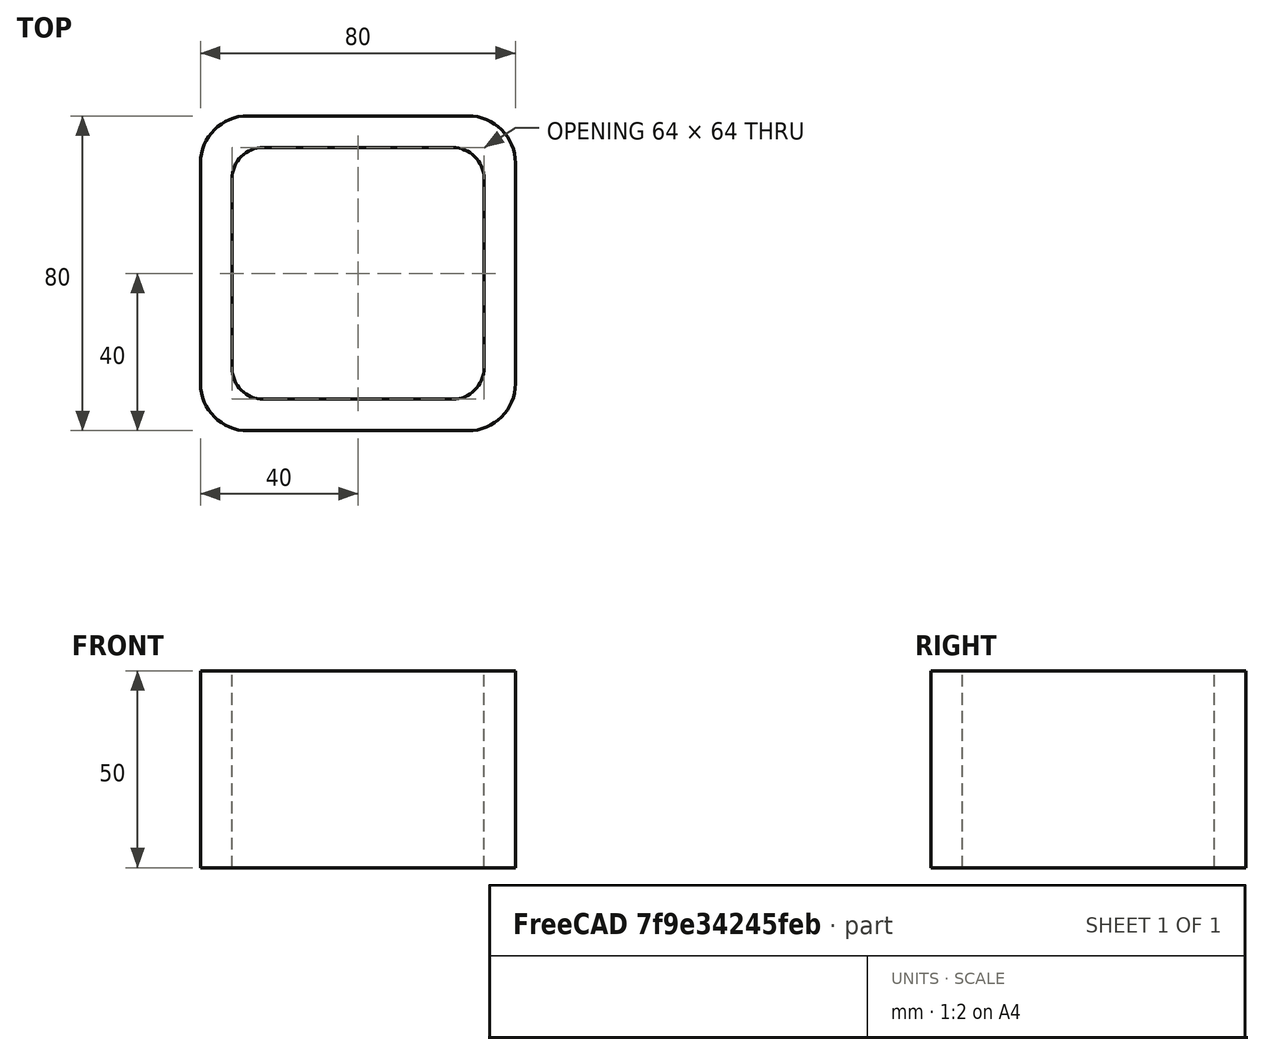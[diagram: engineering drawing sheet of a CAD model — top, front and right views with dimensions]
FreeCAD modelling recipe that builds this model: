
FCSTD DOCUMENT  (FreeCAD 0.15R4671 (Git))
Label: Square hollow section 80x80x8 EN10219 S235JRH
License: All rights reserved
LicenseURL: http://en.wikipedia.org/wiki/All_rights_reserved
objects: Sketcher::SketchObject×1, Part::Extrusion×1
note: 2 computed .brp shape members not serialized (recipe doc carries the construction recipe); baked Part::Feature solids carry a one-line shape summary decoded from their .brp

FEATURE [Sketcher::SketchObject] Sketch
  sketch-geometry (16):
    g0: LineSegment StartX=-24 StartY=32 StartZ=0 EndX=24 EndY=32 EndZ=0
    g1: LineSegment StartX=32 StartY=24 StartZ=0 EndX=32 EndY=-24 EndZ=0
    g2: LineSegment StartX=24 StartY=-32 StartZ=0 EndX=-24 EndY=-32 EndZ=0
    g3: LineSegment StartX=-32 StartY=-24 StartZ=0 EndX=-32 EndY=24 EndZ=0
    g4: LineSegment StartX=-28 StartY=40 StartZ=0 EndX=28 EndY=40 EndZ=0
    g5: LineSegment StartX=40 StartY=28 StartZ=0 EndX=40 EndY=-28 EndZ=0
    g6: LineSegment StartX=28 StartY=-40 StartZ=0 EndX=-28 EndY=-40 EndZ=0
    g7: LineSegment StartX=-40 StartY=-28 StartZ=0 EndX=-40 EndY=28 EndZ=0
    g8: ArcOfCircle CenterX=-24 CenterY=24 CenterZ=0 NormalX=0 NormalY=0 NormalZ=1 Radius=8 StartAngle=1.5708 EndAngle=3.14159
    g9: ArcOfCircle CenterX=24 CenterY=24 CenterZ=0 NormalX=0 NormalY=0 NormalZ=1 Radius=8 StartAngle=0 EndAngle=1.5708
    g10: ArcOfCircle CenterX=24 CenterY=-24 CenterZ=0 NormalX=0 NormalY=0 NormalZ=1 Radius=8 StartAngle=4.71239 EndAngle=6.28319
    g11: ArcOfCircle CenterX=-24 CenterY=-24 CenterZ=0 NormalX=0 NormalY=0 NormalZ=1 Radius=8 StartAngle=3.14159 EndAngle=4.71239
    g12: ArcOfCircle CenterX=28 CenterY=28 CenterZ=0 NormalX=0 NormalY=0 NormalZ=1 Radius=12 StartAngle=0 EndAngle=1.5708
    g13: ArcOfCircle CenterX=28 CenterY=-28 CenterZ=0 NormalX=0 NormalY=0 NormalZ=1 Radius=12 StartAngle=4.71239 EndAngle=6.28319
    g14: ArcOfCircle CenterX=-28 CenterY=-28 CenterZ=0 NormalX=0 NormalY=0 NormalZ=1 Radius=12 StartAngle=3.14159 EndAngle=4.71239
    g15: ArcOfCircle CenterX=-28 CenterY=28 CenterZ=0 NormalX=0 NormalY=0 NormalZ=1 Radius=12 StartAngle=1.5708 EndAngle=3.14159
  constraints (36):
    c: Horizontal(g2)
    c: Vertical(g3)
    c: Horizontal(g6)
    c: Vertical(g7)
    c: Tangent(g3,g8) = 1.5708
    c: Tangent(g0,g8) = 1.5708
    c: Tangent(g0,g9) = 1.5708
    c: Tangent(g1,g9) = 1.5708
    c: Tangent(g1,g10) = 1.5708
    c: Tangent(g2,g10) = 1.5708
    c: Tangent(g2,g11) = 1.5708
    c: Tangent(g3,g11) = 1.5708
    c: Tangent(g4,g12) = 1.5708
    c: Tangent(g5,g12) = 1.5708
    c: Tangent(g5,g13) = 1.5708
    c: Tangent(g6,g13) = 1.5708
    c: Tangent(g6,g14) = 1.5708
    c: Tangent(g7,g14) = 1.5708
    c: Tangent(g7,g15) = 1.5708
    c: Tangent(g4,g15) = 1.5708
    c: Equal(g9,g8)
    c: Equal(g9,g11)
    c: Equal(g9,g10)
    c: Equal(g12,g15)
    c: Equal(g12,g14)
    c: Equal(g12,g13)
    c: Symmetric(g4,g6,g-1)
    c: Symmetric(g7,g5,g-2)
    c: DistanceY(g4,g6) = -80
    c: DistanceX(g7,g5) = 80
    c: Symmetric(g3,g1,g-2)
    c: Symmetric(g0,g2,g-1)
    c: DistanceY(g0,g4) = 8
    c: DistanceX(g5,g1) = -8
    c: Radius(g9) = 8
    c: Radius(g12) = 12
FEATURE [Part::Extrusion] Extrude  label="Square hollow section 80x80x8 EN10219 S235JRH"
  Base = -> Sketch
  Dir = (0,0,50)
  Solid = true
